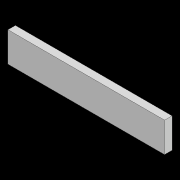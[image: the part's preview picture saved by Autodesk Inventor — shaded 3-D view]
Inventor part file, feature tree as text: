
AUTODESK INVENTOR PART (.ipt)
format: ipt  version: 2021 (Build 250183000, 183)  size: 75,776 bytes
history: native  units: in
note: dims shown in document units (in); Inventor stores cm internally (conversion verified against a paired STEP export)
features: extrude x1, sketch x1
ambient origin geometry x8: Origin, YZ Plane, XZ Plane, XY Plane, X Axis, Y Axis, Z Axis, Center Point
bodies: Solid1 (feature_tree)
feature tree (2):
  extrude  "Extrusion1"  Depth=0.7874in
  sketch  "Sketch1"  dims[d2=4.1339in d3=0.7874in d4=0.1969in d5=0.0in]
